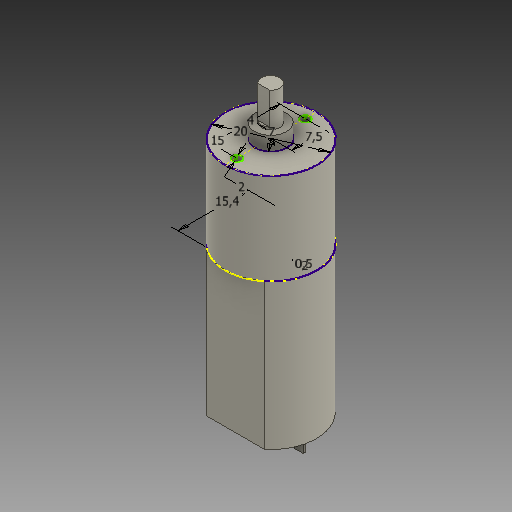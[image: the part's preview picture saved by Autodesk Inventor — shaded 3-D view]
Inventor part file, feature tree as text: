
AUTODESK INVENTOR PART (.ipt)
format: ipt  version: 2020 (Build 240168000, 168)  size: 162,304 bytes
history: native  units: mm
features: extrude x7, sketch x5, hole x2, other x1
ambient origin geometry x8: Origin, YZ Plane, XZ Plane, XY Plane, X Axis, Y Axis, Z Axis, Center Point
bodies: Body1 (feature_tree)
feature tree (15):
  other  "Твердое тело1"
  sketch  "Эскиз1"
  extrude  "Выдавливание1"  Depth=20.0mm
  extrude  "Выдавливание2"  Depth=7.0mm
  extrude  "Выдавливание3"  Depth=4.0mm
  extrude  "Выдавливание4"  Depth=20.0mm TaperAngle=0.0deg
  sketch  "Эскиз3"
  extrude  "Выдавливание5"  Depth=3.0mm TaperAngle=0.0deg
  extrude  "Выдавливание6"  Depth=10.5mm TaperAngle=0.0deg
  extrude  "Выдавливание7"  Depth=1.5mm
  sketch  "Эскиз5"
  hole  "Отверстие1"  [1 undecoded]
  hole  "Отверстие2"  [1 undecoded]
  sketch  "Эскиз2"
  sketch  "Эскиз4"
note: 2 required parameter values undecoded (feature->parameter linkage not recoverable at this tier; creation-order binding heuristic only, values carry confidence <= 0.55)
